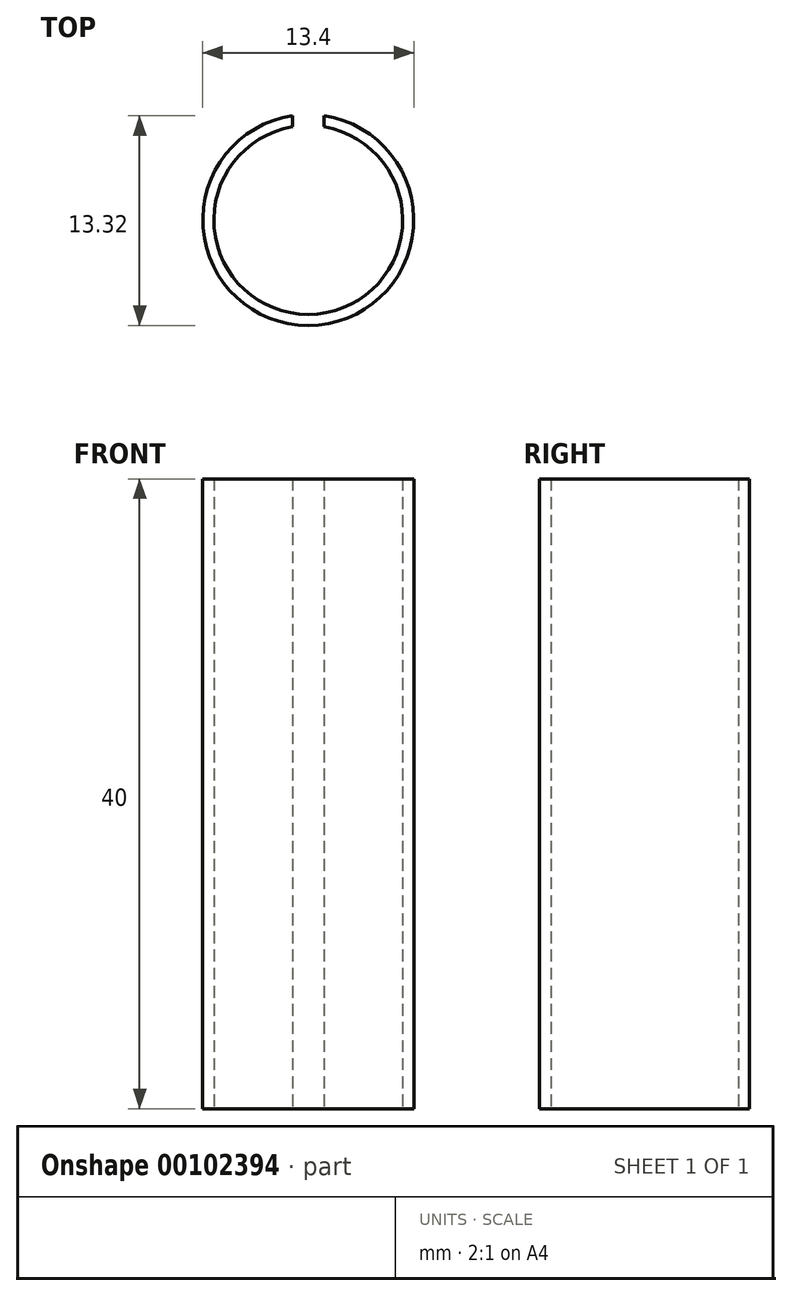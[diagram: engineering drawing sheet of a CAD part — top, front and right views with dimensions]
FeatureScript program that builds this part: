
annotation { "Feature Type Name" : "Feature", "Feature Type Description" : "" }
export const myFeature = defineFeature(function(context is Context, id is Id, definition is map)
    precondition{}
    {
        {
            var Q0;
            Q0=qCreatedBy(makeId("Top.planeOp"),FACE);
            var sketch = newSketch(context, id + "F0", { "sketchPlane" : qUnion([Q0])});
            skCircle(sketch, "E0", {"center": v(0, 0) * mm, "radius": 6.7 * mm});
            skCircle(sketch, "E1", {"center": v(0, 0) * mm, "radius": 6 * mm});
            skSolve(sketch);
        }
        {
            var Q0;
            Q0 = qSketchRegion(id + "F0", true);
            extrude(context, id + "F1", {"entities" : qUnion([Q0]), "depth" : (25 + 15) * mm, "symmetric" : true});
        }
        {
            var Q0;
            Q0=qCreatedBy(makeId("Top.planeOp"),FACE);
            var sketch = newSketch(context, id + "F2", { "sketchPlane" : qUnion([Q0])});
            skLineSegment(sketch, "E2.bottom", {"start": v(-1, 6.7) * mm, "end": v(1, 6.7) * mm});
            skLineSegment(sketch, "E2.top", {"start": v(-1, 0) * mm, "end": v(1, 0) * mm});
            skLineSegment(sketch, "E2.left", {"start": v(-1, 6.7) * mm, "end": v(-1, 0) * mm});
            skLineSegment(sketch, "E2.right", {"start": v(1, 6.7) * mm, "end": v(1, 0) * mm});
            skSolve(sketch);
        }
        {
            var Q0;
            Q0 = qSketchRegion(id + "F2", true);
            extrude(context, id + "F3", {"entities" : qUnion([Q0]), "operationType" : NewBodyOperationType.REMOVE, "endBound" : BoundingType.THROUGH_ALL, "oppositeDirection" : true, "depth" : 25 * mm, "hasSecondDirection" : true, "secondDirectionBound" : BoundingType.THROUGH_ALL, "secondDirectionOppositeDirection" : false, "secondDirectionDepth" : 25 * mm});
        }
    });
